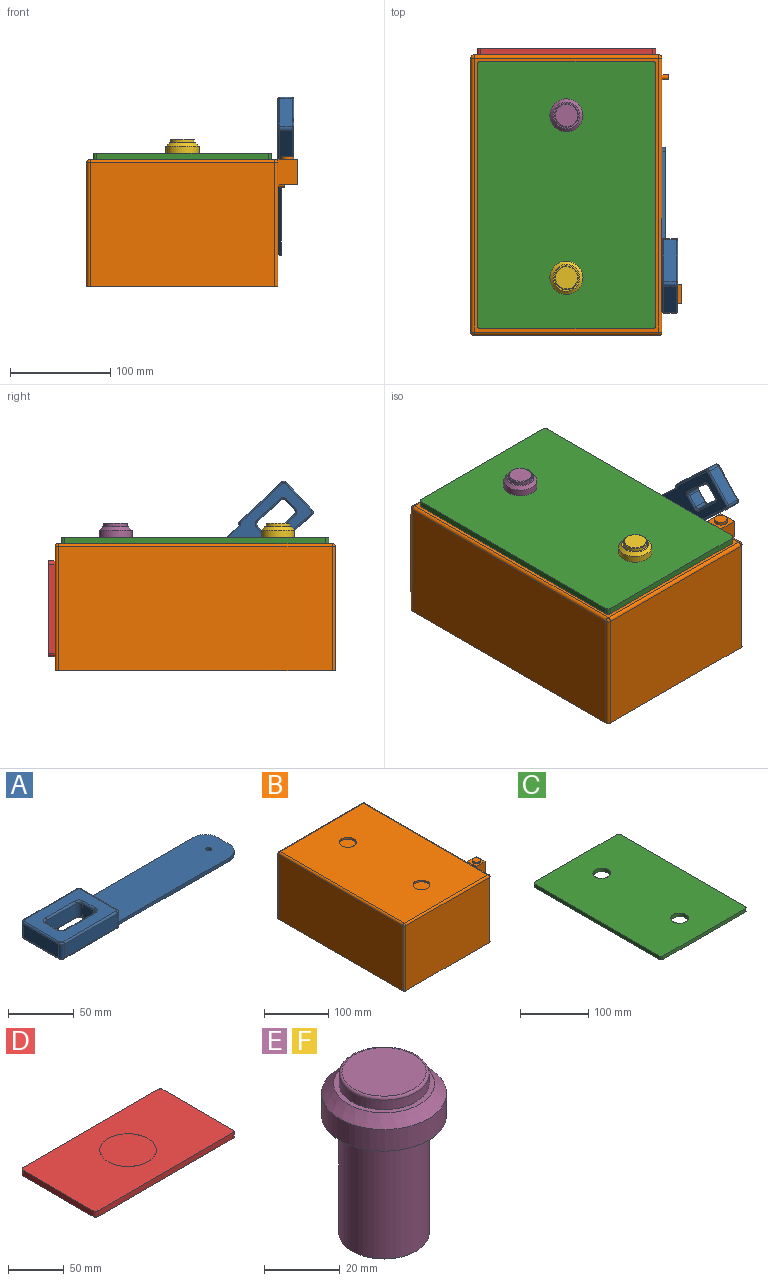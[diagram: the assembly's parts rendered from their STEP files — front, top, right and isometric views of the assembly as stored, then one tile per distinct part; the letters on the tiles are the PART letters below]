
ASSEMBLY  parts=6 mates=5
PART A: 56 faces, bbox 197.1x45x15.9 mm
  f0: cylinder r=1.59mm len=57.15mm, axis (-1,0,0), area 142.5mm2, adj f1,f13,f14,f16
  f1: torus R=1.59mm, axis (0,0,1), area 10.2mm2, adj f0,f2,f13,f17
  f2: cylinder r=1.59mm len=38.1mm, axis (0,-1,0), area 95mm2, adj f1,f3,f13,f18
  f3: torus R=1.59mm, axis (0,0,1), area 10.2mm2, adj f2,f4,f13,f19
  f4: cylinder r=1.59mm len=57.15mm, axis (-1,0,0), area 142.5mm2, adj f3,f13,f15,f20
  f5: cylinder r=1.59mm len=12.7mm, axis (0,-1,0), area 31.7mm2, adj f6,f12,f13,f21
  f6: torus R=4.76mm, axis (0,0,-1), area 14.7mm2, adj f5,f7,f13,f22
  f7: cylinder r=1.59mm len=31.75mm, axis (-1,0,0), area 79.2mm2, adj f6,f8,f13,f23
  f8: torus R=4.76mm, axis (0,0,-1), area 14.7mm2, adj f7,f9,f13,f24
  f9: cylinder r=1.59mm len=12.7mm, axis (0,1,0), area 31.7mm2, adj f8,f10,f13,f25
  f10: torus R=4.76mm, axis (0,0,-1), area 14.7mm2, adj f9,f11,f13,f26
  f11: cylinder r=1.59mm len=31.75mm, axis (1,0,0), area 79.2mm2, adj f10,f12,f13,f27
  f12: torus R=4.76mm, axis (0,0,-1), area 14.7mm2, adj f5,f11,f13,f28
  f13: plane 60.33x41.28mm, normal (0,0,1), area 1589.9mm2, adj f0,f1,f2,f3,f4,f5,f6,f7
  f14: torus R=1.59mm, axis (0,0,1), area 10.2mm2, adj f0,f13,f29,f30
  f15: torus R=1.59mm, axis (0,0,1), area 10.2mm2, adj f4,f13,f29,f31
  f16: plane 57.15x12.7mm, normal (0,1,0), area 725.8mm2, adj f0,f17,f30,f33
  f17: cylinder r=3.17mm len=12.7mm, axis (0,0,1), area 63.3mm2, adj f1,f16,f18,f34
  f18: plane 38.1x12.7mm, normal (-1,0,0), area 483.9mm2, adj f2,f17,f19,f35
  f19: cylinder r=3.17mm len=12.7mm, axis (0,0,-1), area 63.3mm2, adj f3,f18,f20,f36
  f20: plane 57.15x12.7mm, normal (0,-1,0), area 725.8mm2, adj f4,f19,f31,f37
  f21: plane 12.7x12.7mm, normal (-1,0,0), area 161.3mm2, adj f5,f22,f28,f39
  f22: cylinder r=3.17mm len=12.7mm, axis (0,0,-1), area 63.3mm2, adj f6,f21,f23,f40
  f23: plane 31.75x12.7mm, normal (0,1,0), area 403.2mm2, adj f7,f22,f24,f41
  f24: cylinder r=3.17mm len=12.7mm, axis (0,0,-1), area 63.3mm2, adj f8,f23,f25,f42
  f25: plane 12.7x12.7mm, normal (1,0,0), area 161.3mm2, adj f9,f24,f26,f43
  f26: cylinder r=3.17mm len=12.7mm, axis (0,0,-1), area 63.3mm2, adj f10,f25,f27,f44
  f27: plane 31.75x12.7mm, normal (0,-1,0), area 403.2mm2, adj f11,f26,f28,f45
  f28: cylinder r=3.17mm len=12.7mm, axis (0,0,-1), area 63.3mm2, adj f12,f21,f27,f46
  f29: cylinder r=1.59mm len=38.1mm, axis (0,-1,0), area 95mm2, adj f13,f14,f15,f48
  f30: cylinder r=3.17mm len=12.7mm, axis (0,0,1), area 63.3mm2, adj f14,f16,f32,f47,f48
  f31: cylinder r=3.17mm len=12.7mm, axis (0,0,-1), area 63.3mm2, adj f15,f20,f38,f48,f49
  f32: torus R=1.59mm, axis (0,0,1), area 10.2mm2, adj f30,f33,f47,f53
  f33: cylinder r=1.59mm len=57.15mm, axis (-1,0,0), area 142.5mm2, adj f16,f32,f34,f53
  f34: torus R=1.59mm, axis (0,0,1), area 10.2mm2, adj f17,f33,f35,f53
  f35: cylinder r=1.59mm len=38.1mm, axis (0,1,0), area 95mm2, adj f18,f34,f36,f53
  f36: torus R=1.59mm, axis (0,0,1), area 10.2mm2, adj f19,f35,f37,f53
  f37: cylinder r=1.59mm len=57.15mm, axis (-1,0,0), area 142.5mm2, adj f20,f36,f38,f53
  f38: torus R=1.59mm, axis (0,0,1), area 10.2mm2, adj f31,f37,f49,f53
  f39: cylinder r=1.59mm len=12.7mm, axis (0,1,0), area 31.7mm2, adj f21,f40,f46,f53
  f40: torus R=4.76mm, axis (0,0,1), area 14.7mm2, adj f22,f39,f41,f53
  f41: cylinder r=1.59mm len=31.75mm, axis (1,0,0), area 79.2mm2, adj f23,f40,f42,f53
  f42: torus R=4.76mm, axis (0,0,1), area 14.7mm2, adj f24,f41,f43,f53
  f43: cylinder r=1.59mm len=12.7mm, axis (0,-1,0), area 31.7mm2, adj f25,f42,f44,f53
  f44: torus R=4.76mm, axis (0,0,1), area 14.7mm2, adj f26,f43,f45,f53
  f45: cylinder r=1.59mm len=31.75mm, axis (-1,0,0), area 79.2mm2, adj f27,f44,f46,f53
  f46: torus R=4.76mm, axis (0,0,1), area 14.7mm2, adj f28,f39,f45,f53
  f47: plane 122.24x3.18mm, normal (0,1,0), area 383.6mm2, adj f30,f32,f52,f53,f54
  f48: plane 38.1x11.11mm, normal (1,0,0), area 423.4mm2, adj f29,f30,f31,f54
  f49: plane 122.24x3.18mm, normal (0,-1,0), area 383.6mm2, adj f31,f38,f50,f53,f54
  f50: cylinder r=12.7mm len=12.7mm, axis (0,0,1), area 63.3mm2, adj f49,f51,f53,f54
  f51: plane 12.7x3.18mm, normal (1,0,0), area 40.3mm2, adj f50,f52,f53,f54
  f52: cylinder r=12.7mm len=12.7mm, axis (0,0,1), area 63.3mm2, adj f47,f51,f53,f54
  f53: plane 195.26x41.28mm, normal (0,0,-1), area 6645.4mm2, adj f32,f33,f34,f35,f36,f37,f38,f39
  f54: plane 133.35x38.1mm, normal (0,0,1), area 4995mm2, adj f47,f48,f49,f50,f51,f52,f55
  f55: cylinder r=2.29mm len=4.57mm, axis (0,0,-1), area 45.6mm2, adj f53,f54
PART B: 36 faces, bbox 209.6x279.4x130.2 mm
  f0: plane 26.15x26.15mm, normal (0,0,1), area 536.9mm2, adj f5
  f1: plane 26.15x26.15mm, normal (0,0,1), area 536.9mm2, adj f6
  f2: plane 12.7x12.7mm, normal (0,0,1), area 126.7mm2, adj f10
  f3: sphere r=3.17mm, area 15.8mm2, adj f7,f8,f12
  f4: sphere r=3.17mm, area 15.8mm2, adj f8,f9,f14
  f5: cylinder r=13.07mm len=26.15mm, axis (0,0,-1), area 260.8mm2, adj f0,f18
  f6: cylinder r=13.07mm len=26.15mm, axis (0,0,-1), area 260.8mm2, adj f1,f18
  f7: cylinder r=3.17mm len=184.15mm, axis (-1,0,0), area 918.4mm2, adj f3,f16,f17,f18
  f8: cylinder r=3.17mm len=273.05mm, axis (0,-1,0), area 1361.8mm2, adj f3,f4,f13,f18
  f9: cylinder r=3.17mm len=184.15mm, axis (1,0,0), area 918.4mm2, adj f4,f15,f18,f19
  f10: cylinder r=6.35mm len=12.7mm, axis (0,0,1), area 126.7mm2, adj f2,f21
  f11: plane 4.57x4.57mm, normal (1,0,0), area 16.4mm2, adj f24
  f12: cylinder r=3.17mm len=123.83mm, axis (0,0,-1), area 617.5mm2, adj f3,f13,f16,f27
  f13: plane 273.05x123.83mm, normal (-1,0,0), area 33810.4mm2, adj f8,f12,f14,f27
  f14: cylinder r=3.17mm len=123.83mm, axis (0,0,-1), area 617.5mm2, adj f4,f13,f15,f27
  f15: plane 184.15x123.83mm, normal (0,-1,0), area 22802.4mm2, adj f9,f14,f26,f27
  f16: plane 184.15x123.83mm, normal (0,1,0), area 22802.4mm2, adj f7,f12,f27,f28
  f17: sphere r=3.17mm, area 15.8mm2, adj f7,f28,f29
  f18: plane 273.05x184.15mm, normal (0,0,1), area 49208.4mm2, adj f5,f6,f7,f8,f9,f29
  f19: sphere r=3.17mm, area 15.8mm2, adj f9,f26,f29
  f20: plane 19.05x3.18mm, normal (-1,0,0), area 60.5mm2, adj f21,f25,f29,f30
  f21: plane 19.05x19.05mm, normal (0,0,1), area 236.2mm2, adj f10,f20,f22,f25,f30
  f22: plane 25.4x19.05mm, normal (1,0,0), area 483.9mm2, adj f21,f25,f30,f31
  f23: cone r=0.99mm half-angle=59deg, axis (1,0,0), area 14.4mm2, adj f32
  f24: cylinder r=2.29mm len=6.35mm, axis (1,0,0), area 91.2mm2, adj f11,f33
  f25: plane 25.4x19.05mm, normal (0,-1,0), area 483.9mm2, adj f20,f21,f22,f31,f33
  f26: cylinder r=3.17mm len=123.83mm, axis (0,0,-1), area 617.5mm2, adj f15,f19,f27,f33
  f27: plane 279.4x190.5mm, normal (0,0,-1), area 53217mm2, adj f12,f13,f14,f15,f16,f26,f28,f33
  f28: cylinder r=3.17mm len=123.83mm, axis (0,0,-1), area 617.5mm2, adj f16,f17,f27,f33
  f29: cylinder r=3.17mm len=273.05mm, axis (0,1,0), area 1361.8mm2, adj f17,f18,f19,f20,f33
  f30: plane 25.4x19.05mm, normal (0,1,0), area 483.9mm2, adj f20,f21,f22,f31,f33
  f31: plane 19.05x19.05mm, normal (0,0,-1), area 362.9mm2, adj f22,f25,f30,f33
  f32: cylinder r=1.98mm len=25.4mm, axis (-1,0,0), area 316.2mm2, adj f23,f33
  f33: plane 273.05x123.83mm, normal (1,0,0), area 33341.9mm2, adj f24,f25,f26,f27,f28,f29,f30,f31
  f34: plane 4.57x4.57mm, normal (1,0,0), area 16.4mm2, adj f35
  f35: cylinder r=2.29mm len=6.35mm, axis (1,0,0), area 91.2mm2, adj f33,f34
PART C: 12 faces, bbox 177.8x266.7x6.4 mm
  f0: cylinder r=13.07mm len=26.15mm, axis (0,0,1), area 521.6mm2, adj f9,f10
  f1: cylinder r=3.17mm len=6.35mm, axis (0,0,1), area 31.7mm2, adj f2,f8,f9,f10
  f2: plane 260.35x6.35mm, normal (-1,0,0), area 1653.2mm2, adj f1,f3,f9,f10
  f3: cylinder r=3.17mm len=6.35mm, axis (0,0,1), area 31.7mm2, adj f2,f4,f9,f10
  f4: plane 171.45x6.35mm, normal (0,-1,0), area 1088.7mm2, adj f3,f5,f9,f10
  f5: cylinder r=3.17mm len=6.35mm, axis (0,0,1), area 31.7mm2, adj f4,f6,f9,f10
  f6: plane 260.35x6.35mm, normal (1,0,0), area 1653.2mm2, adj f5,f7,f9,f10
  f7: cylinder r=3.17mm len=6.35mm, axis (0,0,1), area 31.7mm2, adj f6,f8,f9,f10
  f8: plane 171.45x6.35mm, normal (0,1,0), area 1088.7mm2, adj f1,f7,f9,f10
  f9: plane 266.7x177.8mm, normal (0,0,1), area 46336.9mm2, adj f0,f1,f2,f3,f4,f5,f6,f7
  f10: plane 266.7x177.8mm, normal (0,0,-1), area 46336.9mm2, adj f0,f1,f2,f3,f4,f5,f6,f7
  f11: cylinder r=13.07mm len=26.15mm, axis (0,0,1), area 521.6mm2, adj f9,f10
PART D: 12 faces, bbox 177.8x95.3x6.4 mm
  f0: plane 177.8x95.25mm, normal (0,0,-1), area 16926.8mm2, adj f1,f2,f3,f4,f5,f6,f7,f8
  f1: cylinder r=3.17mm len=6.35mm, axis (0,0,1), area 31.7mm2, adj f0,f2,f8,f9
  f2: plane 88.9x6.35mm, normal (1,0,0), area 564.5mm2, adj f0,f1,f3,f9
  f3: cylinder r=3.17mm len=6.35mm, axis (0,0,1), area 31.7mm2, adj f0,f2,f4,f9
  f4: plane 171.45x6.35mm, normal (0,1,0), area 1088.7mm2, adj f0,f3,f5,f9
  f5: cylinder r=3.17mm len=6.35mm, axis (0,0,1), area 31.7mm2, adj f0,f4,f6,f9
  f6: plane 88.9x6.35mm, normal (-1,0,0), area 564.5mm2, adj f0,f5,f7,f9
  f7: cylinder r=3.17mm len=6.35mm, axis (0,0,1), area 31.7mm2, adj f0,f6,f8,f9
  f8: plane 171.45x6.35mm, normal (0,-1,0), area 1088.7mm2, adj f0,f1,f7,f9
  f9: plane 177.8x95.25mm, normal (0,0,1), area 14900mm2, adj f1,f2,f3,f4,f5,f6,f7,f8
  f10: plane 50.8x50.8mm, normal (0,0,1), area 2026.8mm2, adj f11
  f11: cylinder r=25.4mm len=50.8mm, axis (0,0,1), area 2mm2, adj f9,f10
PART E: 9 faces, bbox 33x33x52.1 mm
  f0: torus R=11.11mm, axis (0,0,-1), area 87.2mm2, adj f1,f2
  f1: cylinder r=11.87mm len=23.75mm, axis (0,0,-1), area 227.4mm2, adj f0,f4
  f2: plane 22.23x22.23mm, normal (0,0,1), area 387.9mm2, adj f0
  f3: cone r=14.92mm half-angle=45deg, axis (0,0,-1), area 421mm2, adj f4,f5
  f4: plane 26.67x26.67mm, normal (0,0,1), area 115.7mm2, adj f1,f3
  f5: cylinder r=16.51mm len=33.02mm, axis (0,0,-1), area 724.6mm2, adj f3,f8
  f6: cylinder r=11.94mm len=38.1mm, axis (0,0,-1), area 2857.8mm2, adj f7,f8
  f7: plane 23.88x23.88mm, normal (0,0,-1), area 447.7mm2, adj f6
  f8: plane 33.02x33.02mm, normal (0,0,-1), area 408.6mm2, adj f5,f6
PART F: same geometry as E
PLACE A rot(axis=(0.37,0.85,0.37),99.1deg) t=(201.41,171.99,-99.02)mm
PLACE B t=(10.91,5.1,1.93)mm fixed
PLACE C rot(axis=(0,-1,0),180deg) t=(106.16,144.8,8.28)mm
PLACE D rot(axis=(-1,0,0),90deg) t=(10.91,284.5,-133)mm
PLACE E t=(106.16,224.17,22.25)mm
PLACE F t=(106.16,62.25,22.25)mm
MATE fastened B.f16 <-> D.f11  axis (0,1,0) through (106.16,284.5,-63.15)mm
MATE fastened C.f11 <-> E.f0  axis (0,0,1) through (106.16,224.17,8.28)mm
MATE fastened C.f0 <-> B.f6  axis (0,0,-1) through (106.16,62.25,1.93)mm
MATE fastened F.f0 <-> C.f0  axis (0,0,-1) through (106.16,62.25,8.28)mm
MATE revolute B.f23 <-> A.f55  axis (1,0,0) through (201.41,173.37,-74.27)mm
